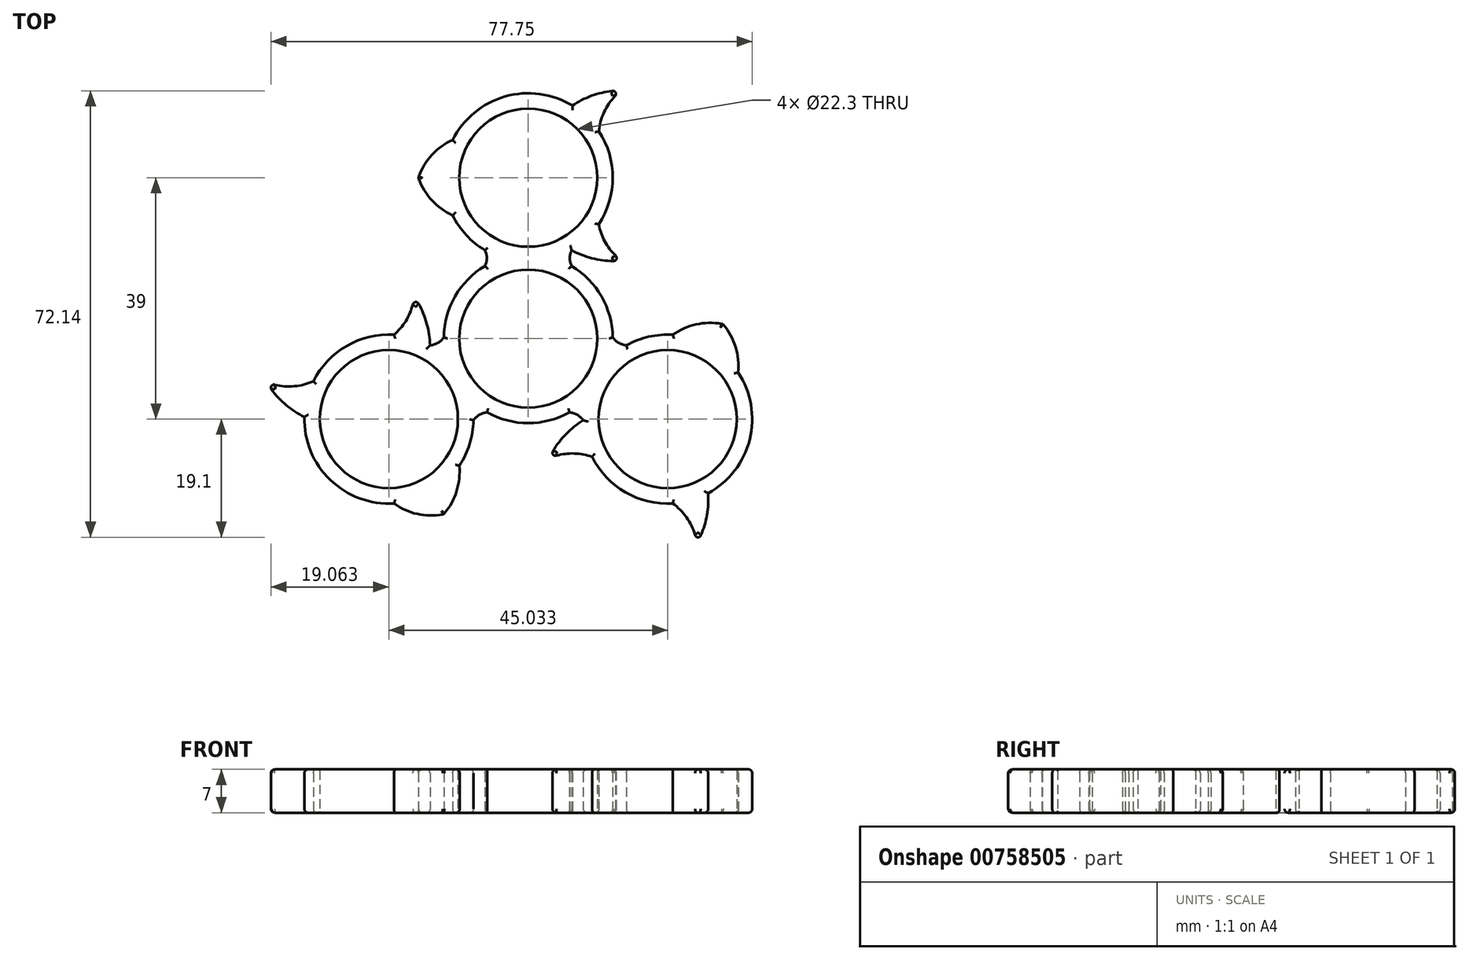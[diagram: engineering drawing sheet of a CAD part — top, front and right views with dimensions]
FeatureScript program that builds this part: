
annotation { "Feature Type Name" : "Feature", "Feature Type Description" : "" }
export const myFeature = defineFeature(function(context is Context, id is Id, definition is map)
    precondition{}
    {
        {
            var Q0;
            Q0=qCreatedBy(makeId("Top.planeOp"),FACE);
            var sketch = newSketch(context, id + "F0", { "sketchPlane" : qUnion([Q0])});
            skCircle(sketch, "E0", {"center": v(0, 0) * mm, "radius": 11.15 * mm});
            skArc(sketch, "E1.0", {"start": v(-5.17, 12.63) * mm, "mid": v(-6.92, 11.76) * mm, "end": v(-8.53, 10.66) * mm, "construction": true});
            skLineSegment(sketch, "E2", {"start": v(0, 0) * mm, "end": v(0, 26) * mm, "construction": true});
            skCircle(sketch, "E3", {"center": v(0, 26) * mm, "radius": 11.15 * mm});
            skArc(sketch, "E4.0", {"start": v(7, 14.28) * mm, "mid": v(0, 39.65) * mm, "end": v(-7, 14.28) * mm});
            skPoint(sketch, "E5.visualSharp", {"position": v(0, 16.7) * mm});
            skLineSegment(sketch, "E6.0", {"start": v(7, 0) * mm, "end": v(7, 29.5) * mm, "construction": true});
            skArc(sketch, "E7.trimOffspring", {"start": v(-7, 11.72) * mm, "mid": v(0, -13.65) * mm, "end": v(7, 11.72) * mm});
            skArc(sketch, "E8", {"start": v(7, 14.28) * mm, "mid": v(6.7, 13) * mm, "end": v(7, 11.72) * mm});
            skArc(sketch, "E9.MirrorCS", {"start": v(-7, 14.28) * mm, "mid": v(-6.7, 13) * mm, "end": v(-7, 11.72) * mm});
            skArc(sketch, "E10", {"start": v(7, 14.28) * mm, "mid": v(10.92, 12.85) * mm, "end": v(15.08, 12.57) * mm});
            skArc(sketch, "E11", {"start": v(11.39, 18.47) * mm, "mid": v(12.67, 15.17) * mm, "end": v(15.08, 12.57) * mm});
            skArc(sketch, "E12.MirrorCS", {"start": v(11.39, 33.38) * mm, "mid": v(12.52, 37.15) * mm, "end": v(15.08, 40.13) * mm});
            skArc(sketch, "E13.MirrorCS", {"start": v(7, 37.57) * mm, "mid": v(10.85, 39.45) * mm, "end": v(15.08, 40.13) * mm});
            skArc(sketch, "E14", {"start": v(-17.74, 26) * mm, "mid": v(-15.6, 22.4) * mm, "end": v(-12.22, 19.91) * mm});
            skArc(sketch, "E15", {"start": v(-12.22, 32.09) * mm, "mid": v(-15.63, 29.63) * mm, "end": v(-17.74, 26) * mm});
            skSolve(sketch);
        }
        {
            var Q0;
            Q0=qSketchRegion(id+"F2",true);
            var Q1;
            Q1=qSketchRegion(id+"F0",true);
            var Q2;
            {var subQ0=sQuery(id+"F0.wireOp",EDGE,"5286eaf0-ed28-4451-94e3-1d908ec19ca7");var subQ1=sQuery(id+"F0.wireOp",EDGE,"E3");var subQ2=makeQuery(id+"F0.imprint","INTERSECT",VERTEX,{"disambiguationData":[OD(0.0)],"derivedFrom":[subQ1,subQ0]});Q2=makeQuery(id+"F0.imprint","IMPRINT",FACE,{"disambiguationData":[TD([[makeQuery(id+"F0.imprint","IMPRINT",EDGE,{"disambiguationData":[TD([[subQ2,-1.0]])],"derivedFrom":subQ1}),-1.0]])]});}
            var Q3;
            {var subQ0=sQuery(id+"F0.wireOp",EDGE,"972e2314-292c-46cc-950a-d2e98ffed2b1");var subQ1=sQuery(id+"F0.wireOp",EDGE,"E3");var subQ2=makeQuery(id+"F0.imprint","INTERSECT",VERTEX,{"disambiguationData":[OD(0.0)],"derivedFrom":[subQ1,subQ0]});Q3=makeQuery(id+"F0.imprint","IMPRINT",FACE,{"disambiguationData":[TD([[makeQuery(id+"F0.imprint","IMPRINT",EDGE,{"disambiguationData":[TD([[subQ2,-1.0]])],"derivedFrom":subQ1}),-1.0]])]});}
            var Q4;
            {var subQ0=sQuery(id+"F0.wireOp",EDGE,"8576df35-fd95-4b7d-8476-f7b5d8a5ebd1");var subQ1=sQuery(id+"F0.wireOp",EDGE,"E3");var subQ2=makeQuery(id+"F0.imprint","INTERSECT",VERTEX,{"disambiguationData":[OD(0.0)],"derivedFrom":[subQ1,subQ0]});Q4=makeQuery(id+"F0.imprint","IMPRINT",FACE,{"disambiguationData":[TD([[makeQuery(id+"F0.imprint","IMPRINT",EDGE,{"disambiguationData":[TD([[subQ2,-1.0]])],"derivedFrom":subQ1}),-1.0]])]});}
            var Q5;
            {var subQ0=sQuery(id+"F0.wireOp",EDGE,"upsWoKqN-qIG4-cDSa-tKJD-hM69GbnP515O");var subQ1=sQuery(id+"F0.wireOp",EDGE,"E3");var subQ2=makeQuery(id+"F0.imprint","INTERSECT",VERTEX,{"disambiguationData":[OD(0.0)],"derivedFrom":[subQ1,subQ0]});Q5=makeQuery(id+"F0.imprint","IMPRINT",FACE,{"disambiguationData":[TD([[makeQuery(id+"F0.imprint","IMPRINT",EDGE,{"disambiguationData":[TD([[subQ2,-1.0]])],"derivedFrom":subQ1}),-1.0]])]});}
            var Q6;
            {var subQ0=sQuery(id+"F0.wireOp",EDGE,"2dc68220-ebba-422f-adc0-bbb553f4a656");var subQ1=sQuery(id+"F0.wireOp",EDGE,"E3");var subQ2=makeQuery(id+"F0.imprint","INTERSECT",VERTEX,{"disambiguationData":[OD(0.0)],"derivedFrom":[subQ1,subQ0]});Q6=makeQuery(id+"F0.imprint","IMPRINT",FACE,{"disambiguationData":[TD([[makeQuery(id+"F0.imprint","IMPRINT",EDGE,{"disambiguationData":[TD([[subQ2,-1.0]])],"derivedFrom":subQ1}),-1.0]])]});}
            var Q7;
            {var subQ0=sQuery(id+"F0.wireOp",EDGE,"70cbc2a9-83ff-4b48-bb73-ff75b1e053e5");var subQ1=sQuery(id+"F0.wireOp",EDGE,"E3");var subQ2=makeQuery(id+"F0.imprint","INTERSECT",VERTEX,{"disambiguationData":[OD(0.0)],"derivedFrom":[subQ1,subQ0]});Q7=makeQuery(id+"F0.imprint","IMPRINT",FACE,{"disambiguationData":[TD([[makeQuery(id+"F0.imprint","IMPRINT",EDGE,{"disambiguationData":[TD([[subQ2,1.0]])],"derivedFrom":subQ1}),-1.0]])]});}
            var Q8;
            {var subQ0=sQuery(id+"F0.wireOp",EDGE,"8457dc48-e8ce-439c-b6e1-438fe0c9034f");var subQ1=sQuery(id+"F0.wireOp",EDGE,"E3");var subQ2=makeQuery(id+"F0.imprint","INTERSECT",VERTEX,{"disambiguationData":[OD(0.0)],"derivedFrom":[subQ1,subQ0]});Q8=makeQuery(id+"F0.imprint","IMPRINT",FACE,{"disambiguationData":[TD([[makeQuery(id+"F0.imprint","IMPRINT",EDGE,{"disambiguationData":[TD([[subQ2,-1.0]])],"derivedFrom":subQ1}),-1.0]])]});}
            var Q9;
            {var subQ0=sQuery(id+"F0.wireOp",EDGE,"6db5ce6a-88a4-4cba-8603-f791245f7d5f");var subQ1=sQuery(id+"F0.wireOp",EDGE,"E3");var subQ2=makeQuery(id+"F0.imprint","INTERSECT",VERTEX,{"disambiguationData":[OD(0.0)],"derivedFrom":[subQ1,subQ0]});Q9=makeQuery(id+"F0.imprint","IMPRINT",FACE,{"disambiguationData":[TD([[makeQuery(id+"F0.imprint","IMPRINT",EDGE,{"disambiguationData":[TD([[subQ2,-1.0]])],"derivedFrom":subQ1}),-1.0]])]});}
            var Q10;
            {var subQ0=sQuery(id+"F0.wireOp",EDGE,"26ba9915-316d-43ac-97a0-efcd31670470");var subQ1=sQuery(id+"F0.wireOp",EDGE,"E3");var subQ2=makeQuery(id+"F0.imprint","INTERSECT",VERTEX,{"disambiguationData":[OD(0.0)],"derivedFrom":[subQ1,subQ0]});Q10=makeQuery(id+"F0.imprint","IMPRINT",FACE,{"disambiguationData":[TD([[makeQuery(id+"F0.imprint","IMPRINT",EDGE,{"disambiguationData":[TD([[subQ2,-1.0]])],"derivedFrom":subQ1}),-1.0]])]});}
            extrude(context, id + "F1", {"entities" : qUnion([Q0, Q1, Q2, Q3, Q4, Q5, Q6, Q7, Q8, Q9, Q10]), "depth" : 7 * mm, "offsetDistance" : 25 * mm});
        }
        {
            var Q0;
            Q0=qCreatedBy(makeId("Right.planeOp"),FACE);
            var sketch = newSketch(context, id + "F2", { "sketchPlane" : qUnion([Q0])});
            skLineSegment(sketch, "E16", {"start": v(0, -11.35) * mm, "end": v(0, 14.45) * mm, "construction": true});
            skSolve(sketch);
        }
        {
            var Q0;
            Q0=makeQuery(id+"F1.opExtrude","SWEPT_FACE",FACE,{"disambiguationData":[OSD([sQuery(id+"F0.wireOp",EDGE,"E0")])]});
            var Q1;
            Q1=makeQuery(id+"F1.opExtrude","SWEPT_FACE",FACE,{"disambiguationData":[OSD([sQuery(id+"F0.wireOp",EDGE,"E3")])]});
            fillet(context, id + "F3", {"entities" : qUnion([Q0, Q1]), "radius" : 0.2 * mm, "tangentPropagation" : true, "allowEdgeOverflow" : false});
        }
        {
            var Q0;
            Q0=makeQuery(id+"F1.opExtrude","SWEPT_EDGE",EDGE,{"disambiguationData":[OSD([sQuery(id+"F0.wireOp",EDGE,"B6IW4b8f-rdPB-c0Us-c8Mo-Mq4TzhgtsJ4K"),sQuery(id+"F0.wireOp",EDGE,"YkMFX2vO-4Crt-TsgE-euFS-UGkuE4yFQV92")])]});
            var Q1;
            Q1=makeQuery(id+"F1.opExtrude","SWEPT_EDGE",EDGE,{"disambiguationData":[OSD([sQuery(id+"F0.wireOp",EDGE,"05Ssocvi-DhHh-OsZG-e2E6-rp3hOyrowWxE"),sQuery(id+"F0.wireOp",EDGE,"gXTc2K6m-pDrj-VkwX-DA3g-2FsoQV2dXgWA")])]});
            var Q2;
            Q2=makeQuery(id+"F1.opExtrude","SWEPT_EDGE",EDGE,{"disambiguationData":[OSD([sQuery(id+"F0.wireOp",EDGE,"WV1YJwpc-lhCt-Tkbw-pyGD-IAguLvoMxcio"),sQuery(id+"F0.wireOp",EDGE,"lRAOphcG-mkQV-B9rX-murS-RDVpryX3sv7Y")])]});
            var Q3;
            Q3=makeQuery(id+"F1.opExtrude","CAP_FACE",FACE,{"disambiguationData":[OSD([sQuery(id+"F0.wireOp",EDGE,"E0"),sQuery(id+"F0.wireOp",EDGE,"E3"),sQuery(id+"F0.wireOp",EDGE,"E4.0"),sQuery(id+"F0.wireOp",EDGE,"E7.trimOffspring"),sQuery(id+"F0.wireOp",EDGE,"E8"),sQuery(id+"F0.wireOp",EDGE,"E9.MirrorCS"),sQuery(id+"F0.wireOp",EDGE,"A4q6XAE9-nX4I-gney-ZS84-N0PxHdFMNtC2"),sQuery(id+"F0.wireOp",EDGE,"90f88150-1d21-4d5f-99c7-c443b2953583"),sQuery(id+"F0.wireOp",EDGE,"aea63897-bdd4-478d-acf8-b9e86850efd0"),sQuery(id+"F0.wireOp",EDGE,"e52c3788-5800-4ccf-9de2-e600990ce032"),sQuery(id+"F0.wireOp",EDGE,"6943e6b1-6e27-4218-960a-470c6ffbd814"),sQuery(id+"F0.wireOp",EDGE,"dd87b57e-f014-4439-b0ae-6b8a5318a583"),sQuery(id+"F0.wireOp",EDGE,"9d18db76-b666-4d6e-9b71-35c6185a29a1")])],"isStart":false});
            var Q4;
            Q4=makeQuery(id+"F1.opExtrude","CAP_FACE",FACE,{"disambiguationData":[OSD([sQuery(id+"F0.wireOp",EDGE,"E0"),sQuery(id+"F0.wireOp",EDGE,"E3"),sQuery(id+"F0.wireOp",EDGE,"E4.0"),sQuery(id+"F0.wireOp",EDGE,"E7.trimOffspring"),sQuery(id+"F0.wireOp",EDGE,"E8"),sQuery(id+"F0.wireOp",EDGE,"E9.MirrorCS"),sQuery(id+"F0.wireOp",EDGE,"A4q6XAE9-nX4I-gney-ZS84-N0PxHdFMNtC2"),sQuery(id+"F0.wireOp",EDGE,"90f88150-1d21-4d5f-99c7-c443b2953583"),sQuery(id+"F0.wireOp",EDGE,"aea63897-bdd4-478d-acf8-b9e86850efd0"),sQuery(id+"F0.wireOp",EDGE,"e52c3788-5800-4ccf-9de2-e600990ce032"),sQuery(id+"F0.wireOp",EDGE,"6943e6b1-6e27-4218-960a-470c6ffbd814"),sQuery(id+"F0.wireOp",EDGE,"dd87b57e-f014-4439-b0ae-6b8a5318a583"),sQuery(id+"F0.wireOp",EDGE,"9d18db76-b666-4d6e-9b71-35c6185a29a1")])],"isStart":true});
            fillet(context, id + "F4", {"entities" : qUnion([Q0, Q1, Q2, Q3, Q4]), "radius" : 0.6 * mm, "tangentPropagation" : true, "allowEdgeOverflow" : false});
        }
        {
            var Q0;
            Q0=makeQuery(id+"F1.opExtrude","SWEPT_BODY",BODY,{"disambiguationData":[OSD([sQuery(id+"F0.wireOp",EDGE,"E0"),sQuery(id+"F0.wireOp",EDGE,"E1.0"),sQuery(id+"F0.wireOp",EDGE,"E3"),sQuery(id+"F0.wireOp",EDGE,"E4.0"),sQuery(id+"F0.wireOp",EDGE,"7c884c8c-e37f-41f7-9a8e-9150e4511ce8.0"),sQuery(id+"F0.wireOp",EDGE,"124d70be-8a2f-4ff1-8067-023c3a760d13.0"),sQuery(id+"F0.wireOp",EDGE,"7qioyo7K-iHsX-Xa6s-X97m-BwtuQXfGrCvp"),sQuery(id+"F0.wireOp",EDGE,"oFAU7C9Q-nsB6-dseo-MMuZ-7hNLlDQCrwbt"),sQuery(id+"F0.wireOp",EDGE,"a2486781-22df-47b1-8026-fe576fbc433f.0"),sQuery(id+"F0.wireOp",EDGE,"cb9c9ce2-17e4-408e-8bf5-b38f411324f0.0"),sQuery(id+"F0.wireOp",EDGE,"jKmUo85i-UXFQ-YKQP-mafa-QPdGbBQ2pSZu"),sQuery(id+"F0.wireOp",EDGE,"14rnQz0T-OoW9-SuH9-BmvN-4Fd0IeYT7QfG")])]});
            var Q1;
            Q1=sQuery(id+"F2.wireOp",EDGE,"E16");
            circularPattern(context, id + "F5", {"operationType" : NewBodyOperationType.ADD, "entities" : qUnion([Q0]), "axis" : qUnion([Q1]), "angle" : 360 * degree, "instanceCount" : 3, "equalSpace" : true});
        }
        {
            var Q0;
            Q0=makeQuery(id+"F1.opExtrude","SWEPT_EDGE",EDGE,{"disambiguationData":[OSD([sQuery(id+"F0.wireOp",EDGE,"E12.MirrorCS"),sQuery(id+"F0.wireOp",EDGE,"E13.MirrorCS")])]});
            var Q1;
            Q1=makeQuery(id+"F1.opExtrude","SWEPT_EDGE",EDGE,{"disambiguationData":[OSD([sQuery(id+"F0.wireOp",EDGE,"E10"),sQuery(id+"F0.wireOp",EDGE,"E11")])]});
            var Q2;
            Q2=makeQuery(id+"F1.opExtrude","SWEPT_EDGE",EDGE,{"disambiguationData":[OSD([sQuery(id+"F0.wireOp",EDGE,"E14"),sQuery(id+"F0.wireOp",EDGE,"E15")])]});
            var Q3;
            Q3=makeQuery(id+"F5.opPattern","COPY",EDGE,{"derivedFrom":makeQuery(id+"F1.opExtrude","SWEPT_EDGE",EDGE,{"disambiguationData":[OSD([sQuery(id+"F0.wireOp",EDGE,"E10"),sQuery(id+"F0.wireOp",EDGE,"E11")])]}),"instanceName":"1"});
            var Q4;
            Q4=makeQuery(id+"F5.opPattern","COPY",EDGE,{"derivedFrom":makeQuery(id+"F1.opExtrude","SWEPT_EDGE",EDGE,{"disambiguationData":[OSD([sQuery(id+"F0.wireOp",EDGE,"E12.MirrorCS"),sQuery(id+"F0.wireOp",EDGE,"E13.MirrorCS")])]}),"instanceName":"1"});
            var Q5;
            Q5=makeQuery(id+"F5.opPattern","COPY",EDGE,{"derivedFrom":makeQuery(id+"F1.opExtrude","SWEPT_EDGE",EDGE,{"disambiguationData":[OSD([sQuery(id+"F0.wireOp",EDGE,"E14"),sQuery(id+"F0.wireOp",EDGE,"E15")])]}),"instanceName":"1"});
            var Q6;
            Q6=makeQuery(id+"F5.opPattern","COPY",EDGE,{"derivedFrom":makeQuery(id+"F1.opExtrude","SWEPT_EDGE",EDGE,{"disambiguationData":[OSD([sQuery(id+"F0.wireOp",EDGE,"E10"),sQuery(id+"F0.wireOp",EDGE,"E11")])]}),"instanceName":"2"});
            var Q7;
            Q7=makeQuery(id+"F5.opPattern","COPY",EDGE,{"derivedFrom":makeQuery(id+"F1.opExtrude","SWEPT_EDGE",EDGE,{"disambiguationData":[OSD([sQuery(id+"F0.wireOp",EDGE,"E14"),sQuery(id+"F0.wireOp",EDGE,"E15")])]}),"instanceName":"2"});
            var Q8;
            Q8=makeQuery(id+"F5.opPattern","COPY",EDGE,{"derivedFrom":makeQuery(id+"F1.opExtrude","SWEPT_EDGE",EDGE,{"disambiguationData":[OSD([sQuery(id+"F0.wireOp",EDGE,"E12.MirrorCS"),sQuery(id+"F0.wireOp",EDGE,"E13.MirrorCS")])]}),"instanceName":"2"});
            fillet(context, id + "F6", {"entities" : qUnion([Q0, Q1, Q2, Q3, Q4, Q5, Q6, Q7, Q8]), "radius" : .5 * mm, "tangentPropagation" : true, "allowEdgeOverflow" : false});
        }
    });
